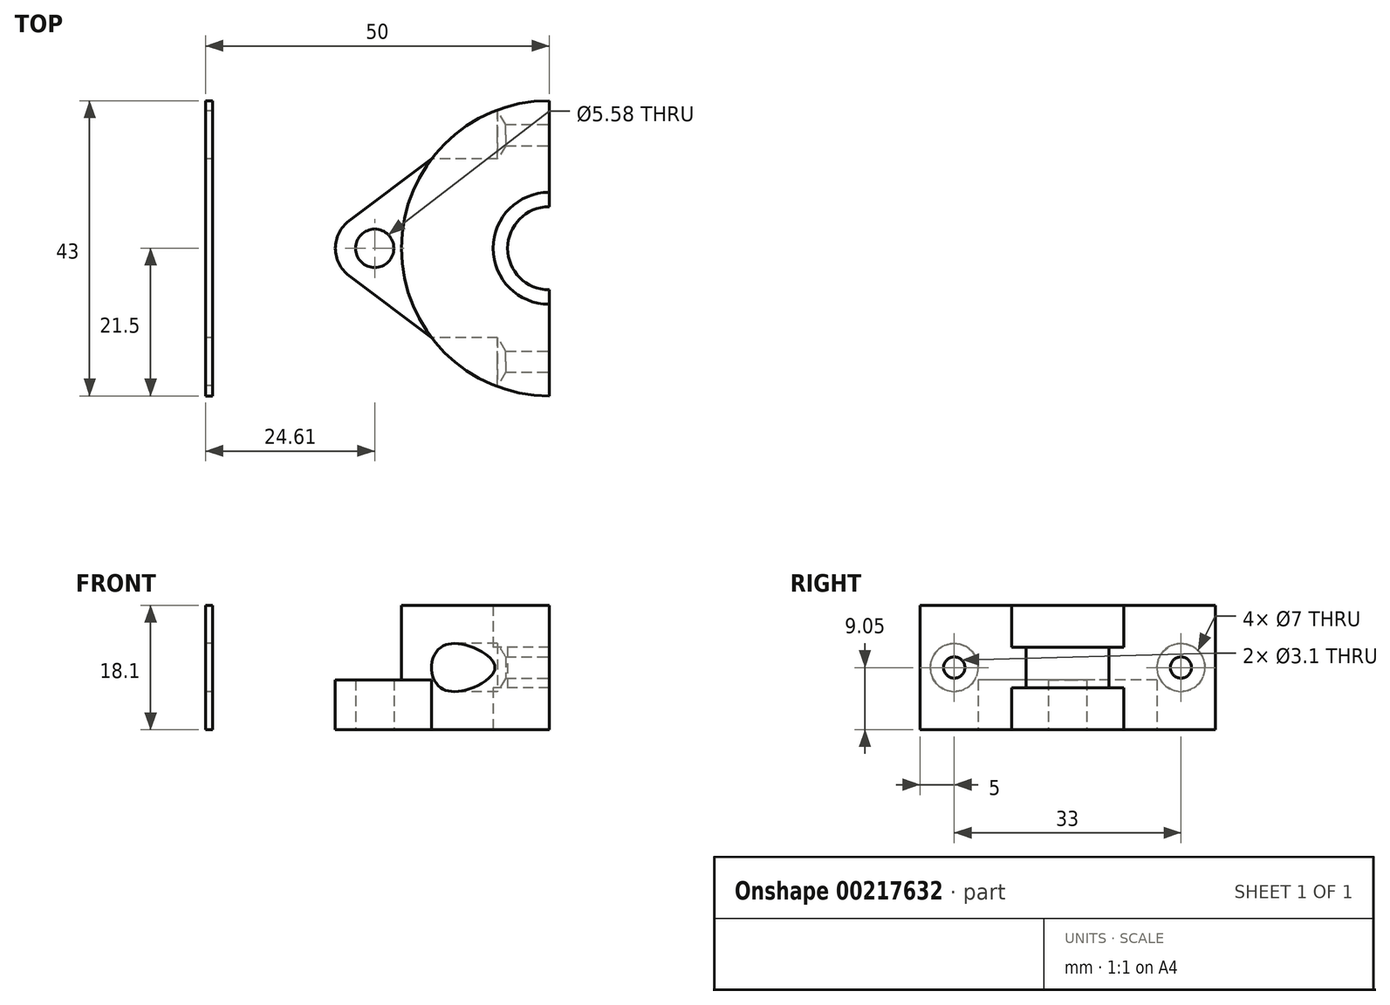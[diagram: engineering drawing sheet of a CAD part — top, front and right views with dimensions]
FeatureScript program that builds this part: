
annotation { "Feature Type Name" : "Feature", "Feature Type Description" : "" }
export const myFeature = defineFeature(function(context is Context, id is Id, definition is map)
    precondition{}
    {
        {
            var Q0;
            Q0=qCreatedBy(makeId("Top.planeOp"),FACE);
            var sketch = newSketch(context, id + "F0", { "sketchPlane" : qUnion([Q0])});
            skCircle(sketch, "E0", {"center": v(0, 0) * mm, "radius": 21.5 * mm});
            skCircle(sketch, "E1", {"center": v(0, 0) * mm, "radius": 8.15 * mm});
            skCircle(sketch, "E2", {"center": v(0, 0) * mm, "radius": 6.05 * mm});
            skCircle(sketch, "E3", {"center": v(-25.4, 0) * mm, "radius": 2.8 * mm});
            skCircle(sketch, "E4", {"center": v(25.4, 0) * mm, "radius": 2.8 * mm});
            skLineSegment(sketch, "E5", {"start": v(-17.12, 13) * mm, "end": v(-29.12, 4) * mm});
            skLineSegment(sketch, "E6", {"start": v(-29.12, 4) * mm, "end": v(-29.12, -4) * mm});
            skLineSegment(sketch, "E7", {"start": v(-29.12, -4) * mm, "end": v(-17.12, -13) * mm});
            skArc(sketch, "E8", {"start": v(-29.12, 4) * mm, "mid": v(-31.12, 0) * mm, "end": v(-29.12, -4) * mm});
            skLineSegment(sketch, "E9", {"start": v(0, 0) * mm, "end": v(0, 21.5) * mm});
            skLineSegment(sketch, "E10", {"start": v(0, 0) * mm, "end": v(0, -21.5) * mm});
            skLineSegment(sketch, "E11", {"start": v(17.12, 13) * mm, "end": v(29.12, 4) * mm});
            skLineSegment(sketch, "E12", {"start": v(29.12, 4) * mm, "end": v(29.12, -4) * mm});
            skLineSegment(sketch, "E13", {"start": v(29.12, -4) * mm, "end": v(17.12, -13) * mm});
            skArc(sketch, "E14", {"start": v(29.12, -4) * mm, "mid": v(31.12, 0) * mm, "end": v(29.12, 4) * mm});
            skLineSegment(sketch, "E15.bottom", {"start": v(-50, 21.5) * mm, "end": v(-49, 21.5) * mm});
            skLineSegment(sketch, "E15.top", {"start": v(-50, -21.5) * mm, "end": v(-49, -21.5) * mm});
            skLineSegment(sketch, "E15.left", {"start": v(-50, 21.5) * mm, "end": v(-50, -21.5) * mm});
            skLineSegment(sketch, "E15.right", {"start": v(-49, 21.5) * mm, "end": v(-49, -21.5) * mm});
            skSolve(sketch);
        }
        {
            var Q0;
            {var subQ5=sQuery(id+"F0.wireOp",EDGE,"E0");var subQ8=makeQuery(id+"F0.imprint","INTERSECT",VERTEX,{"derivedFrom":[subQ5,sQuery(id+"F0.wireOp",EDGE,"E5")]});Q0=makeQuery(id+"F0.imprint","IMPRINT",FACE,{"disambiguationData":[TD([[makeQuery(id+"F0.imprint","IMPRINT",EDGE,{"disambiguationData":[TD([[subQ8,1.0]])],"derivedFrom":subQ5}),1.0]])]});}
            extrude(context, id + "F1", {"entities" : qUnion([Q0]), "depth" : 18.1 * mm});
        }
        {
            var Q0;
            {var subQ0=sQuery(id+"F0.wireOp",EDGE,"E9");var subQ1=sQuery(id+"F0.wireOp",EDGE,"E1");var subQ2=makeQuery(id+"F0.imprint","INTERSECT",VERTEX,{"derivedFrom":[subQ1,subQ0]});Q0=makeQuery(id+"F0.imprint","IMPRINT",FACE,{"disambiguationData":[TD([[makeQuery(id+"F0.imprint","IMPRINT",EDGE,{"disambiguationData":[TD([[subQ2,-1.0]])],"derivedFrom":subQ1}),1.0]])]});}
            extrude(context, id + "F2", {"entities" : qUnion([Q0]), "operationType" : NewBodyOperationType.ADD, "depth" : 11.97 * mm, "hasSecondDirection" : true, "secondDirectionOppositeDirection" : false, "secondDirectionDepth" : 6.12 * mm});
        }
        {
            var Q0;
            Q0=makeQuery(id+"F0.imprint","IMPRINT",FACE,{"disambiguationData":[TD([[makeQuery(id+"F0.imprint","IMPRINT",EDGE,{"derivedFrom":sQuery(id+"F0.wireOp",EDGE,"E3")}),-1.0]])]});
            var Q1;
            Q1=makeQuery(id+"F0.imprint","IMPRINT",FACE,{"disambiguationData":[TD([[makeQuery(id+"F0.imprint","IMPRINT",EDGE,{"derivedFrom":sQuery(id+"F0.wireOp",EDGE,"E6")}),-1.0]])]});
            extrude(context, id + "F3", {"entities" : qUnion([Q0, Q1]), "operationType" : NewBodyOperationType.ADD, "depth" : 7.25 * mm});
        }
        {
            var Q0;
            {var subQ0=sQuery(id+"F0.wireOp",EDGE,"E10");Q0=makeQuery(id+"F2.boolean.opBoolean","MERGE",FACE,{"derivedFrom":[makeQuery(id+"F1.opExtrude","SWEPT_FACE",FACE,{"disambiguationData":[OSD([subQ0])]}),makeQuery(id+"F2.opExtrude","SWEPT_FACE",FACE,{"disambiguationData":[OSD([subQ0])]})]});}
            var sketch = newSketch(context, id + "F4", { "sketchPlane" : qUnion([Q0])});
            skCircle(sketch, "E16", {"center": v(-16.5, 9.05) * mm, "radius": 1.5 * mm});
            skCircle(sketch, "E17", {"center": v(16.5, 9.05) * mm, "radius": 1.5 * mm});
            skSolve(sketch);
        }
        {
            var Q0;
            Q0=sQuery(id+"F4.wireOp",VERTEX,"E16.center");
            var Q1;
            Q1=sQuery(id+"F4.wireOp",VERTEX,"E17.center");
            var Q2;
            Q2=makeQuery(id+"F1.opExtrude","SWEPT_BODY",BODY,{"disambiguationData":[OSD([sQuery(id+"F0.wireOp",EDGE,"E0"),sQuery(id+"F0.wireOp",EDGE,"E1"),sQuery(id+"F0.wireOp",EDGE,"E9"),sQuery(id+"F0.wireOp",EDGE,"E10")])]});
            hole(context, id + "F5", {"style" : HoleStyle.SIMPLE, "endStyle" : HoleEndStyle.THROUGH, "holeDiameter" : 3.1 * mm, "startFromSketch" : true, "locations" : qUnion([Q0, Q1]), "scope" : qUnion([Q2]), "isTappedThrough" : true});
        }
        {
            var Q0;
            Q0=makeQuery(id+"F0.imprint","IMPRINT",FACE,{"disambiguationData":[TD([[makeQuery(id+"F0.imprint","IMPRINT",EDGE,{"derivedFrom":sQuery(id+"F0.wireOp",EDGE,"E15.bottom")}),-1.0]])]});
            extrude(context, id + "F6", {"entities" : qUnion([Q0]), "depth" : 18.1 * mm});
        }
        {
            var Q0;
            Q0=makeQuery(id+"F6.opExtrude","SWEPT_FACE",FACE,{"disambiguationData":[OSD([sQuery(id+"F0.wireOp",EDGE,"E15.left")])]});
            var sketch = newSketch(context, id + "F7", { "sketchPlane" : qUnion([Q0])});
            skCircle(sketch, "E18", {"center": v(-16.5, 9.05) * mm, "radius": 3.5 * mm});
            skCircle(sketch, "E19", {"center": v(16.5, 9.05) * mm, "radius": 3.5 * mm});
            skSolve(sketch);
        }
        {
            var Q0;
            Q0=sQuery(id+"F7.wireOp",VERTEX,"E18.center");
            var Q1;
            Q1=sQuery(id+"F7.wireOp",VERTEX,"E19.center");
            var Q2;
            Q2=makeQuery(id+"F1.opExtrude","SWEPT_BODY",BODY,{"disambiguationData":[OSD([sQuery(id+"F0.wireOp",EDGE,"E0"),sQuery(id+"F0.wireOp",EDGE,"E1"),sQuery(id+"F0.wireOp",EDGE,"E9"),sQuery(id+"F0.wireOp",EDGE,"E10")])]});
            var Q3;
            Q3=makeQuery(id+"F6.opExtrude","SWEPT_BODY",BODY,{"disambiguationData":[OSD([sQuery(id+"F0.wireOp",EDGE,"E15.bottom"),sQuery(id+"F0.wireOp",EDGE,"E15.top"),sQuery(id+"F0.wireOp",EDGE,"E15.left"),sQuery(id+"F0.wireOp",EDGE,"E15.right")])]});
            hole(context, id + "F8", {"style" : HoleStyle.SIMPLE, "endStyle" : HoleEndStyle.BLIND, "holeDiameter" : 7 * mm, "holeDepth" : 42.5 * mm, "startFromSketch" : true, "locations" : qUnion([Q0, Q1]), "scope" : qUnion([Q2, Q3])});
        }
    });
